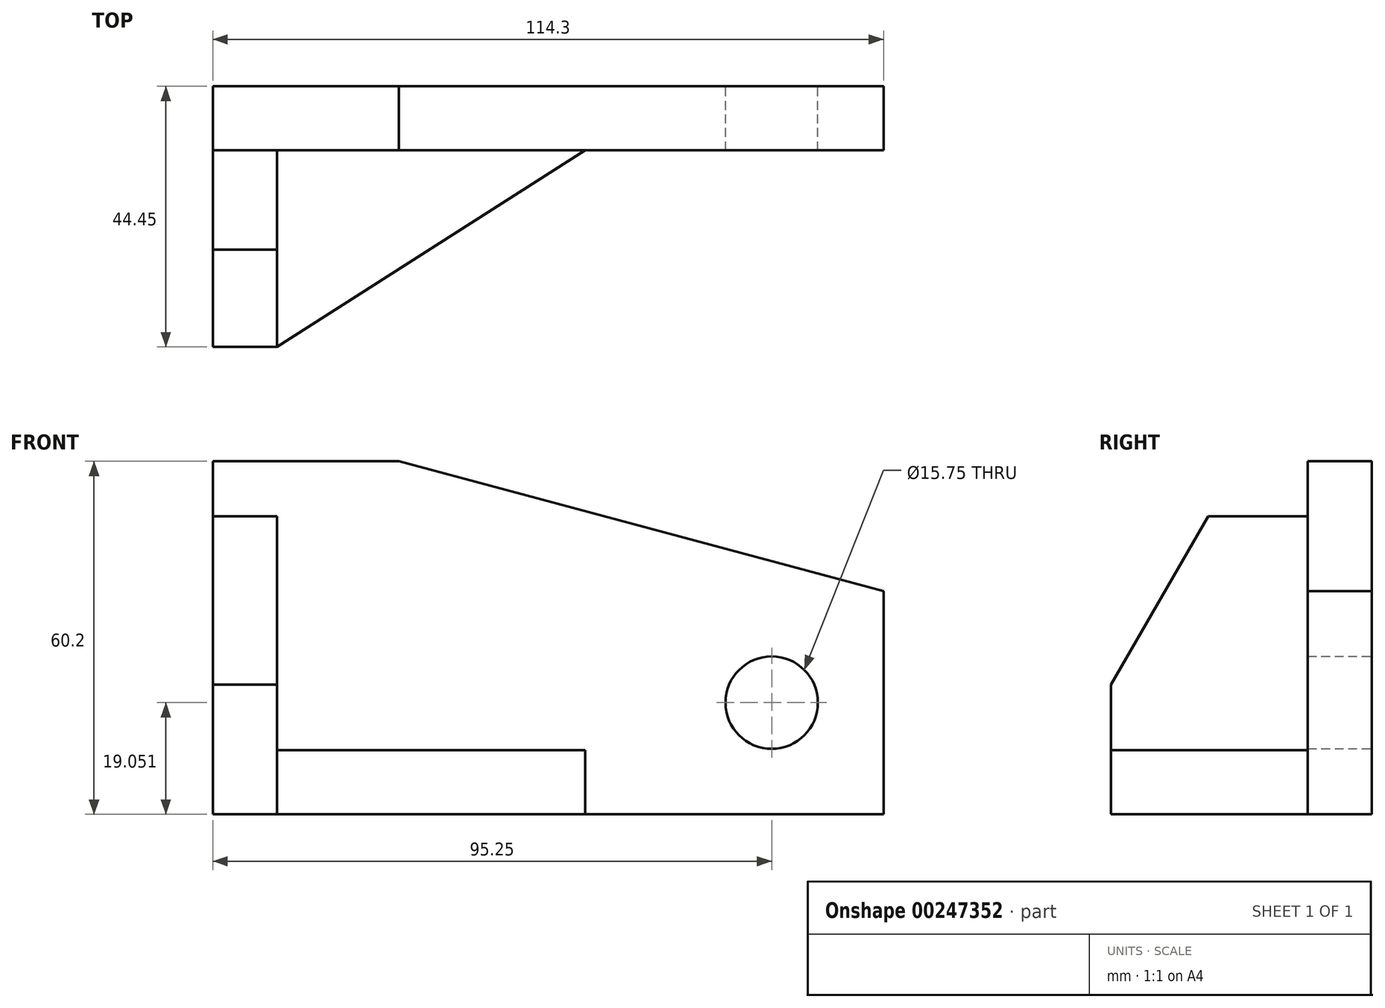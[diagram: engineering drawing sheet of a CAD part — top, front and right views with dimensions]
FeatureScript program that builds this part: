
annotation { "Feature Type Name" : "Feature", "Feature Type Description" : "" }
export const myFeature = defineFeature(function(context is Context, id is Id, definition is map)
    precondition{}
    {
        {
            var Q0;
            Q0=qCreatedBy(makeId("Front.planeOp"),FACE);
            var sketch = newSketch(context, id + "F0", { "sketchPlane" : qUnion([Q0])});
            skLineSegment(sketch, "E0.bottom", {"start": v(0, 30.1) * mm, "end": v(31.75, 30.1) * mm});
            skLineSegment(sketch, "E0.top", {"start": v(0, -30.1) * mm, "end": v(114.3, -30.1) * mm});
            skLineSegment(sketch, "E0.left", {"start": v(0, 30.1) * mm, "end": v(0, -30.1) * mm});
            skLineSegment(sketch, "E0.right", {"start": v(114.3, 7.98) * mm, "end": v(114.3, -30.1) * mm});
            skLineSegment(sketch, "E1", {"start": v(31.75, 30.1) * mm, "end": v(114.3, 7.98) * mm});
            skCircle(sketch, "E2", {"center": v(95.25, -11.05) * mm, "radius": 7.87 * mm});
            skSolve(sketch);
        }
        {
            var Q0;
            Q0=makeQuery(id+"F0.imprint","IMPRINT",FACE,{"disambiguationData":[TD([[makeQuery(id+"F0.imprint","IMPRINT",EDGE,{"derivedFrom":sQuery(id+"F0.wireOp",EDGE,"E0.bottom")}),-1.0]])]});
            var Q1;
            {var subQ4=sQuery(id+"F0.wireOp",EDGE,"NYAMkGFi-PALX-9JL6-yMBU-7D1fSY5vlQhd");Q1=makeQuery(id+"F0.imprint","IMPRINT",FACE,{"disambiguationData":[TD([[makeQuery(id+"F0.imprint","IMPRINT",EDGE,{"derivedFrom":subQ4}),-1.0]])]});}
            extrude(context, id + "F1", {"entities" : qUnion([Q0, Q1]), "depth" : 10.92 * mm});
        }
        {
            var Q0;
            Q0=makeQuery(id+"F1.opExtrude","CAP_FACE",FACE,{"disambiguationData":[OSD([sQuery(id+"F0.wireOp",EDGE,"E0.bottom"),sQuery(id+"F0.wireOp",EDGE,"E0.top"),sQuery(id+"F0.wireOp",EDGE,"E0.left"),sQuery(id+"F0.wireOp",EDGE,"E0.right"),sQuery(id+"F0.wireOp",EDGE,"E1"),sQuery(id+"F0.wireOp",EDGE,"E2")])],"isStart":false});
            var sketch = newSketch(context, id + "F2", { "sketchPlane" : qUnion([Q0])});
            skLineSegment(sketch, "E3.bottom", {"start": v(0, 20.7) * mm, "end": v(10.92, 20.7) * mm});
            skLineSegment(sketch, "E3.top", {"start": v(0, -30.1) * mm, "end": v(10.92, -30.1) * mm});
            skLineSegment(sketch, "E3.left", {"start": v(0, 20.7) * mm, "end": v(0, -30.1) * mm});
            skLineSegment(sketch, "E3.right", {"start": v(10.92, 20.7) * mm, "end": v(10.92, -30.1) * mm});
            skSolve(sketch);
        }
        {
            var Q0;
            Q0=makeQuery(id+"F2.imprint","IMPRINT",FACE,{"disambiguationData":[TD([[makeQuery(id+"F2.imprint","IMPRINT",EDGE,{"derivedFrom":sQuery(id+"F2.wireOp",EDGE,"E3.bottom")}),-1.0]])]});
            extrude(context, id + "F3", {"entities" : qUnion([Q0]), "operationType" : NewBodyOperationType.ADD, "depth" : 33.53 * mm});
        }
        {
            var Q0;
            Q0=makeQuery(id+"F3.opExtrude","SWEPT_FACE",FACE,{"disambiguationData":[OSD([sQuery(id+"F2.wireOp",EDGE,"E3.right")])]});
            var sketch = newSketch(context, id + "F4", { "sketchPlane" : qUnion([Q0])});
            skLineSegment(sketch, "E4", {"start": v(-27.88, 20.7) * mm, "end": v(-44.45, -8) * mm});
            skSolve(sketch);
        }
        {
            var Q0;
            {var subQ0=sQuery(id+"F4.wireOp",EDGE,"E4");Q0=makeQuery(id+"F4.imprint","IMPRINT",FACE,{"disambiguationData":[TD([[makeQuery(id+"F4.imprint","IMPRINT",EDGE,{"derivedFrom":subQ0}),-1.0]])]});}
            extrude(context, id + "F5", {"entities" : qUnion([Q0]), "operationType" : NewBodyOperationType.REMOVE, "endBound" : BoundingType.THROUGH_ALL, "oppositeDirection" : true, "depth" : 25.4 * mm});
        }
        {
            var Q0;
            Q0=makeQuery(id+"F3.boolean.opBoolean","MERGE",FACE,{"derivedFrom":[makeQuery(id+"F1.opExtrude","SWEPT_FACE",FACE,{"disambiguationData":[OSD([sQuery(id+"F0.wireOp",EDGE,"E0.top")])]}),makeQuery(id+"F3.opExtrude","SWEPT_FACE",FACE,{"disambiguationData":[OSD([sQuery(id+"F2.wireOp",EDGE,"E3.top")])]})]});
            var sketch = newSketch(context, id + "F6", { "sketchPlane" : qUnion([Q0])});
            skLineSegment(sketch, "E5", {"start": v(10.92, 44.45) * mm, "end": v(63.5, 10.92) * mm});
            skSolve(sketch);
        }
        {
            var Q0;
            {var subQ0=sQuery(id+"F6.wireOp",EDGE,"E5");Q0=makeQuery(id+"F6.imprint","IMPRINT",FACE,{"disambiguationData":[TD([[makeQuery(id+"F6.imprint","IMPRINT",EDGE,{"derivedFrom":subQ0}),-1.0]])]});}
            extrude(context, id + "F7", {"entities" : qUnion([Q0]), "operationType" : NewBodyOperationType.ADD, "oppositeDirection" : true, "depth" : 10.92 * mm});
        }
    });
